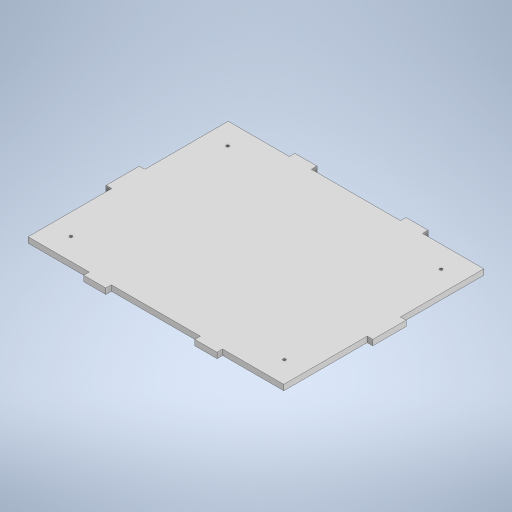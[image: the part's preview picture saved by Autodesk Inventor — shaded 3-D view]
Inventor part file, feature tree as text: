
AUTODESK INVENTOR PART (.ipt)
format: ipt  version: 2023 (Build 270158000, 158)  size: 275,456 bytes
history: native  units: mm
features: sketch x4, extrude x3, hole x1
ambient origin geometry x8: Origin, YZ Plane, XZ Plane, XY Plane, X Axis, Y Axis, Z Axis, Center Point
bodies: Solid1 (feature_tree)
feature tree (8):
  extrude  "Extrusion1"  Depth=230.0mm
  extrude  "Extrusion2"  Depth=20.0mm
  extrude  "Extrusion3"  Depth=80.0mm
  hole  "Hole1"  [1 undecoded]
  sketch  "Sketch1"  dims[d0=180.0mm d1=230.0mm]
  sketch  "Sketch2"  dims[d2=5.0mm d3=0.0mm d4=20.0mm]
  sketch  "Sketch3"  dims[d5=20.0mm d6=80.0mm]
  sketch  "Sketch4"  dims[d7=55.0mm d8=55.0mm d9=5.0mm d10=185.0mm d11=0.0mm d12=0.0mm d13=30.0mm d14=75.0mm d15=5.0mm d16=235.0mm d17=0.0mm d18=0.0mm d19=141.0mm d20=192.0mm d21=19.0mm d22=141.0mm d23=0.0mm d24=19.5mm d25=2.459mm d26=4.0mm d27=4.0mm d28=2.0mm d29=90.0deg d30=8.0mm d31=20.594885mm]
note: 1 required parameter value undecoded (feature->parameter linkage not recoverable at this tier; creation-order binding heuristic only, values carry confidence <= 0.55)
